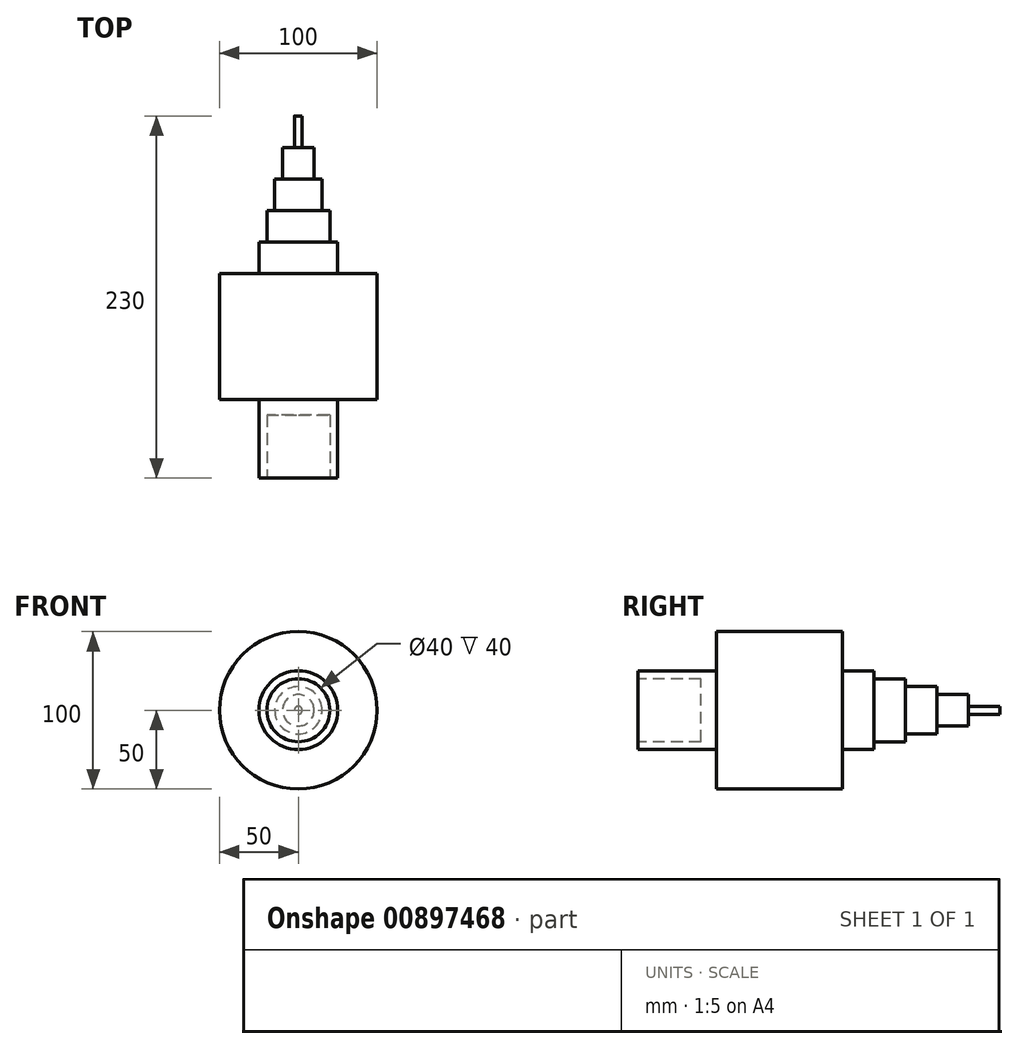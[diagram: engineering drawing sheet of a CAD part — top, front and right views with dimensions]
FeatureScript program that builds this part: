
annotation { "Feature Type Name" : "Feature", "Feature Type Description" : "" }
export const myFeature = defineFeature(function(context is Context, id is Id, definition is map)
    precondition{}
    {
        {
            var Q0;
            Q0=qCreatedBy(makeId("Front.planeOp"),FACE);
            var sketch = newSketch(context, id + "F0", { "sketchPlane" : qUnion([Q0])});
            skCircle(sketch, "E0", {"center": v(0, 0) * mm, "radius": 50 * mm});
            skSolve(sketch);
        }
        {
            var Q0;
            Q0=makeQuery(id+"F0.imprint","IMPRINT",FACE,{"disambiguationData":[TD([[makeQuery(id+"F0.imprint","IMPRINT",EDGE,{"derivedFrom":sQuery(id+"F0.wireOp",EDGE,"E0")}),1.0]])]});
            extrude(context, id + "F1", {"entities" : qUnion([Q0]), "depth" : 80 * mm, "offsetDistance" : 25.4 * mm});
        }
        {
            var Q0;
            Q0=makeQuery(id+"F1.opExtrude","CAP_FACE",FACE,{"disambiguationData":[OSD([sQuery(id+"F0.wireOp",EDGE,"E0")])],"isStart":false});
            var sketch = newSketch(context, id + "F2", { "sketchPlane" : qUnion([Q0])});
            skCircle(sketch, "E1", {"center": v(0, 0) * mm, "radius": 25 * mm});
            skSolve(sketch);
        }
        {
            var Q0;
            Q0=makeQuery(id+"F2.imprint","IMPRINT",FACE,{"disambiguationData":[TD([[makeQuery(id+"F2.imprint","IMPRINT",EDGE,{"derivedFrom":sQuery(id+"F2.wireOp",EDGE,"E1")}),1.0]])]});
            extrude(context, id + "F3", {"entities" : qUnion([Q0]), "operationType" : NewBodyOperationType.ADD, "depth" : 50 * mm, "offsetDistance" : 25.4 * mm});
        }
        {
            var Q0;
            Q0=makeQuery(id+"F3.opExtrude","CAP_FACE",FACE,{"disambiguationData":[OSD([sQuery(id+"F2.wireOp",EDGE,"E1")])],"isStart":false});
            var sketch = newSketch(context, id + "F4", { "sketchPlane" : qUnion([Q0])});
            skCircle(sketch, "E2", {"center": v(0, 0) * mm, "radius": 20 * mm});
            skSolve(sketch);
        }
        {
            var Q0;
            Q0=makeQuery(id+"F4.imprint","IMPRINT",FACE,{"disambiguationData":[TD([[makeQuery(id+"F4.imprint","IMPRINT",EDGE,{"derivedFrom":sQuery(id+"F4.wireOp",EDGE,"E2")}),1.0]])]});
            extrude(context, id + "F5", {"entities" : qUnion([Q0]), "operationType" : NewBodyOperationType.REMOVE, "oppositeDirection" : true, "depth" : 40 * mm, "offsetDistance" : 25.4 * mm});
        }
        {
            var Q0;
            Q0=makeQuery(id+"F1.opExtrude","CAP_FACE",FACE,{"disambiguationData":[OSD([sQuery(id+"F0.wireOp",EDGE,"E0")])],"isStart":true});
            var sketch = newSketch(context, id + "F6", { "sketchPlane" : qUnion([Q0])});
            skCircle(sketch, "E3", {"center": v(0, 0) * mm, "radius": 25 * mm});
            skSolve(sketch);
        }
        {
            var Q0;
            Q0=makeQuery(id+"F6.imprint","IMPRINT",FACE,{"disambiguationData":[TD([[makeQuery(id+"F6.imprint","IMPRINT",EDGE,{"derivedFrom":sQuery(id+"F6.wireOp",EDGE,"E3")}),1.0]])]});
            extrude(context, id + "F7", {"entities" : qUnion([Q0]), "operationType" : NewBodyOperationType.ADD, "depth" : 20 * mm, "offsetDistance" : 25.4 * mm});
        }
        {
            var Q0;
            Q0=makeQuery(id+"F7.opExtrude","CAP_FACE",FACE,{"disambiguationData":[OSD([sQuery(id+"F6.wireOp",EDGE,"E3")])],"isStart":false});
            var sketch = newSketch(context, id + "F8", { "sketchPlane" : qUnion([Q0])});
            skCircle(sketch, "E4", {"center": v(0, 0) * mm, "radius": 20 * mm});
            skSolve(sketch);
        }
        {
            var Q0;
            Q0=makeQuery(id+"F8.imprint","IMPRINT",FACE,{"disambiguationData":[TD([[makeQuery(id+"F8.imprint","IMPRINT",EDGE,{"derivedFrom":sQuery(id+"F8.wireOp",EDGE,"E4")}),1.0]])]});
            extrude(context, id + "F9", {"entities" : qUnion([Q0]), "operationType" : NewBodyOperationType.ADD, "depth" : 20 * mm, "offsetDistance" : 25.4 * mm});
        }
        {
            var Q0;
            Q0=makeQuery(id+"F9.opExtrude","CAP_FACE",FACE,{"disambiguationData":[OSD([sQuery(id+"F8.wireOp",EDGE,"E4")])],"isStart":false});
            var sketch = newSketch(context, id + "F10", { "sketchPlane" : qUnion([Q0])});
            skCircle(sketch, "E5", {"center": v(0, 0) * mm, "radius": 15 * mm});
            skSolve(sketch);
        }
        {
            var Q0;
            Q0=makeQuery(id+"F10.imprint","IMPRINT",FACE,{"disambiguationData":[TD([[makeQuery(id+"F10.imprint","IMPRINT",EDGE,{"derivedFrom":sQuery(id+"F10.wireOp",EDGE,"E5")}),1.0]])]});
            extrude(context, id + "F11", {"entities" : qUnion([Q0]), "operationType" : NewBodyOperationType.ADD, "depth" : 20 * mm, "offsetDistance" : 25.4 * mm});
        }
        {
            var Q0;
            Q0=makeQuery(id+"F11.opExtrude","CAP_FACE",FACE,{"disambiguationData":[OSD([sQuery(id+"F10.wireOp",EDGE,"E5")])],"isStart":false});
            var sketch = newSketch(context, id + "F12", { "sketchPlane" : qUnion([Q0])});
            skCircle(sketch, "E6", {"center": v(0, 0) * mm, "radius": 10 * mm});
            skSolve(sketch);
        }
        {
            var Q0;
            Q0=makeQuery(id+"F12.imprint","IMPRINT",FACE,{"disambiguationData":[TD([[makeQuery(id+"F12.imprint","IMPRINT",EDGE,{"derivedFrom":sQuery(id+"F12.wireOp",EDGE,"E6")}),1.0]])]});
            extrude(context, id + "F13", {"entities" : qUnion([Q0]), "operationType" : NewBodyOperationType.ADD, "depth" : 20 * mm, "offsetDistance" : 25.4 * mm});
        }
        {
            var Q0;
            Q0=makeQuery(id+"F13.opExtrude","CAP_FACE",FACE,{"disambiguationData":[OSD([sQuery(id+"F12.wireOp",EDGE,"E6")])],"isStart":false});
            var sketch = newSketch(context, id + "F14", { "sketchPlane" : qUnion([Q0])});
            skCircle(sketch, "E7", {"center": v(0, 0) * mm, "radius": 2.5 * mm});
            skSolve(sketch);
        }
        {
            var Q0;
            Q0=makeQuery(id+"F14.imprint","IMPRINT",FACE,{"disambiguationData":[TD([[makeQuery(id+"F14.imprint","IMPRINT",EDGE,{"derivedFrom":sQuery(id+"F14.wireOp",EDGE,"E7")}),1.0]])]});
            extrude(context, id + "F15", {"entities" : qUnion([Q0]), "operationType" : NewBodyOperationType.ADD, "depth" : 20 * mm, "offsetDistance" : 25.4 * mm});
        }
    });
